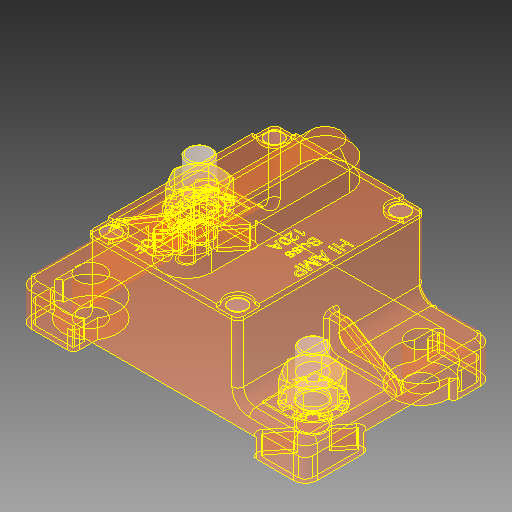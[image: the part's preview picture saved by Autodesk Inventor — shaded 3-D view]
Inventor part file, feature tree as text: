
AUTODESK INVENTOR PART (.ipt)
format: ipt  version: 2019 (Build 230136000, 136)  size: 1,691,136 bytes
history: native  units: in
note: dims shown in document units (in); Inventor stores cm internally (conversion verified against a paired STEP export)
features: other x2, sketch x1
ambient origin geometry x8: Origin, YZ Plane, XZ Plane, XY Plane, X Axis, Y Axis, Z Axis, Center Point
bodies: Body1 (feature_tree), Body2 (feature_tree), Body3 (feature_tree), Body4 (feature_tree), Body5 (feature_tree), Body6 (feature_tree), Body7 (feature_tree), Body8 (feature_tree), Body9 (feature_tree), Body10 (feature_tree), Body11 (feature_tree), Body12 (feature_tree), Body13 (feature_tree), Body14 (feature_tree), Body15 (feature_tree), Body16 (feature_tree)
feature tree (3):
  sketch  "Sketch1"  dims[d0=2.25in d1=1.1in d2=0.27in d3=2.9in d4=1.9in]
  other  "Composite1"
  other  "Srf1"
